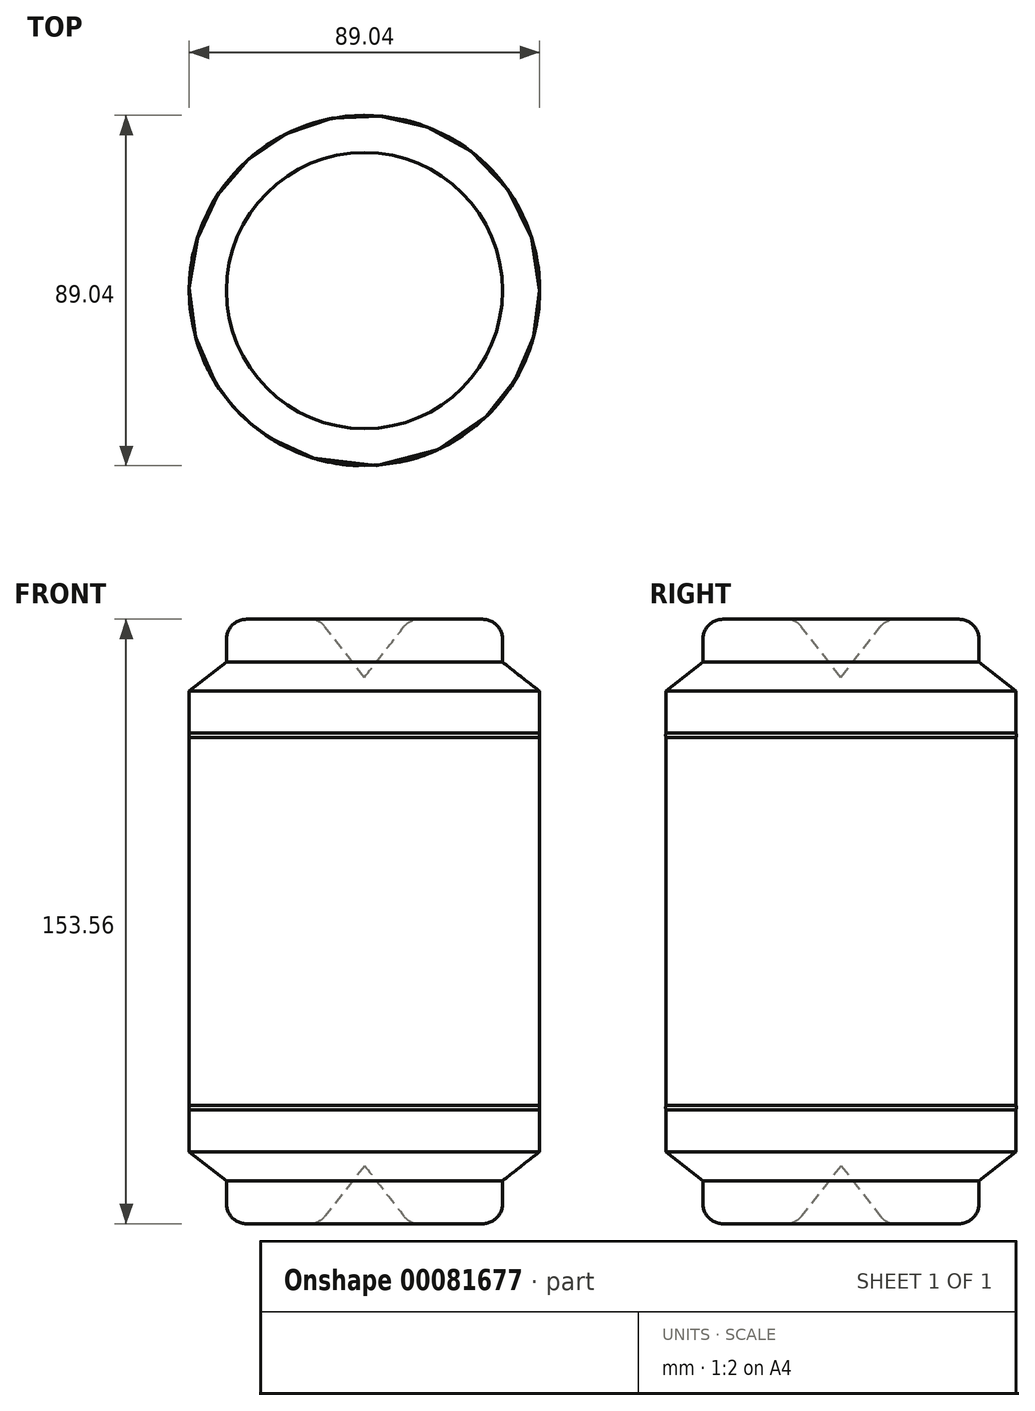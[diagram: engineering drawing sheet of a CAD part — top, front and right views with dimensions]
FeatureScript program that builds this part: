
annotation { "Feature Type Name" : "Feature", "Feature Type Description" : "" }
export const myFeature = defineFeature(function(context is Context, id is Id, definition is map)
    precondition{}
    {
        {
            var Q0;
            Q0=qCreatedBy(makeId("Front.planeOp"),FACE);
            var sketch = newSketch(context, id + "F0", { "sketchPlane" : qUnion([Q0])});
            skLineSegment(sketch, "E0", {"start": v(0, 62.04) * mm, "end": v(0, -61.16) * mm});
            skLineSegment(sketch, "E1", {"start": v(0, -61.16) * mm, "end": v(-30.65, -61.16) * mm});
            skArc(sketch, "E2", {"start": v(-30.65, -61.16) * mm, "mid": v(-40.66, -56.9) * mm, "end": v(-44.5, -46.72) * mm});
            skLineSegment(sketch, "E3", {"start": v(-44.5, -46.72) * mm, "end": v(-44.5, 58.5) * mm});
            skLineSegment(sketch, "E4", {"start": v(-44.5, 58.5) * mm, "end": v(-35.07, 65.87) * mm});
            skLineSegment(sketch, "E5", {"start": v(-35.07, 65.87) * mm, "end": v(-35.07, 76.78) * mm});
            skLineSegment(sketch, "E6", {"start": v(-35.07, 76.78) * mm, "end": v(-11.5, 76.78) * mm});
            skLineSegment(sketch, "E7", {"start": v(-11.5, 76.78) * mm, "end": v(0, 62.04) * mm});
            skSolve(sketch);
        }
        {
            var Q0;
            Q0=makeQuery(id+"F0.imprint","IMPRINT",FACE,{"disambiguationData":[TD([[makeQuery(id+"F0.imprint","IMPRINT",EDGE,{"derivedFrom":sQuery(id+"F0.wireOp",EDGE,"E0")}),-1.0]])]});
            var Q1;
            Q1=sQuery(id+"F0.wireOp",EDGE,"E0");
            revolve(context, id + "F1", {"entities" : qUnion([Q0]), "axis" : qUnion([Q1]), "revolveType" : RevolveType.FULL});
        }
        {
            var Q0;
            Q0=makeQuery(id+"F1.opRevolve","SWEPT_FACE",FACE,{"disambiguationData":[OSD([sQuery(id+"F0.wireOp",EDGE,"E6")])]});
            fillet(context, id + "F2", {"entities" : qUnion([Q0]), "radius" : 5.08 * mm, "tangentPropagation" : true, "allowEdgeOverflow" : false});
        }
        {
            var Q0;
            Q0=makeQuery(id+"F1.opRevolve","SWEPT_BODY",BODY,{"disambiguationData":[OSD([sQuery(id+"F0.wireOp",EDGE,"E0"),sQuery(id+"F0.wireOp",EDGE,"E1"),sQuery(id+"F0.wireOp",EDGE,"E2"),sQuery(id+"F0.wireOp",EDGE,"E3"),sQuery(id+"F0.wireOp",EDGE,"E4"),sQuery(id+"F0.wireOp",EDGE,"E5"),sQuery(id+"F0.wireOp",EDGE,"E6"),sQuery(id+"F0.wireOp",EDGE,"E7")])]});
            var Q1;
            Q1=qCreatedBy(makeId("Top.planeOp"),FACE);
            mirror(context, id + "F3", {"operationType" : NewBodyOperationType.ADD, "entities" : qUnion([Q0]), "mirrorPlane" : qUnion([Q1])});
        }
    });
